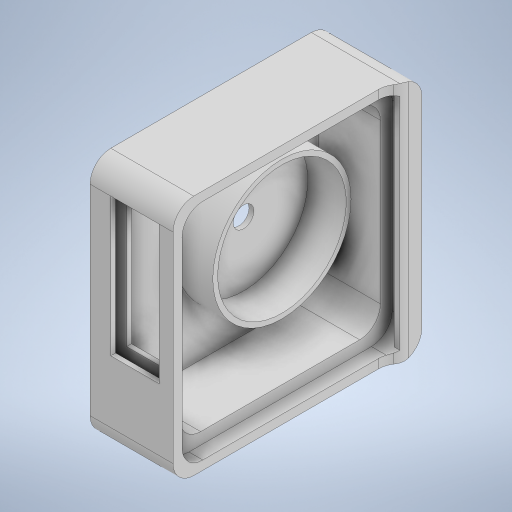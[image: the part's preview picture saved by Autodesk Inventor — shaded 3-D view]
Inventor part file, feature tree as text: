
AUTODESK INVENTOR PART (.ipt)
format: ipt  version: 2024 (Build 280153000, 153)  size: 381,952 bytes
history: native  units: mm
features: sketch x9, extrude x8, other x2, fillet x2, shell x1
ambient origin geometry x8: Origin, YZ Plane, XZ Plane, XY Plane, X Axis, Y Axis, Z Axis, Center Point
bodies: Body1 (feature_tree)
feature tree (22):
  other  "断面1"
  other  "ソリッド1"
  extrude  "押し出し1"  Depth=35.0mm
  extrude  "押し出し2"  Depth=35.0mm
  extrude  "押し出し3"  Depth=12.0mm TaperAngle=0.0deg
  extrude  "押し出し4"  Depth=32.4mm
  shell  "シェル1"  Thickness=32.4mm
  extrude  "押し出し5"  Depth=2.0mm TaperAngle=0.0deg
  extrude  "押し出し6"  Depth=29.0mm
  sketch  "スケッチ10"
  extrude  "押し出し7"  Depth=29.0mm
  fillet  "フィレット1"  Radius=9.0mm
  fillet  "フィレット2"  Radius=20.0mm
  extrude  "押し出し8"  Depth=5.25mm TaperAngle=0.0deg
  sketch  "スケッチ1"
  sketch  "スケッチ2"
  sketch  "スケッチ3"
  sketch  "スケッチ4"
  sketch  "スケッチ6"
  sketch  "スケッチ9"
  sketch  "スケッチ11"
  sketch  "スケッチ12"
